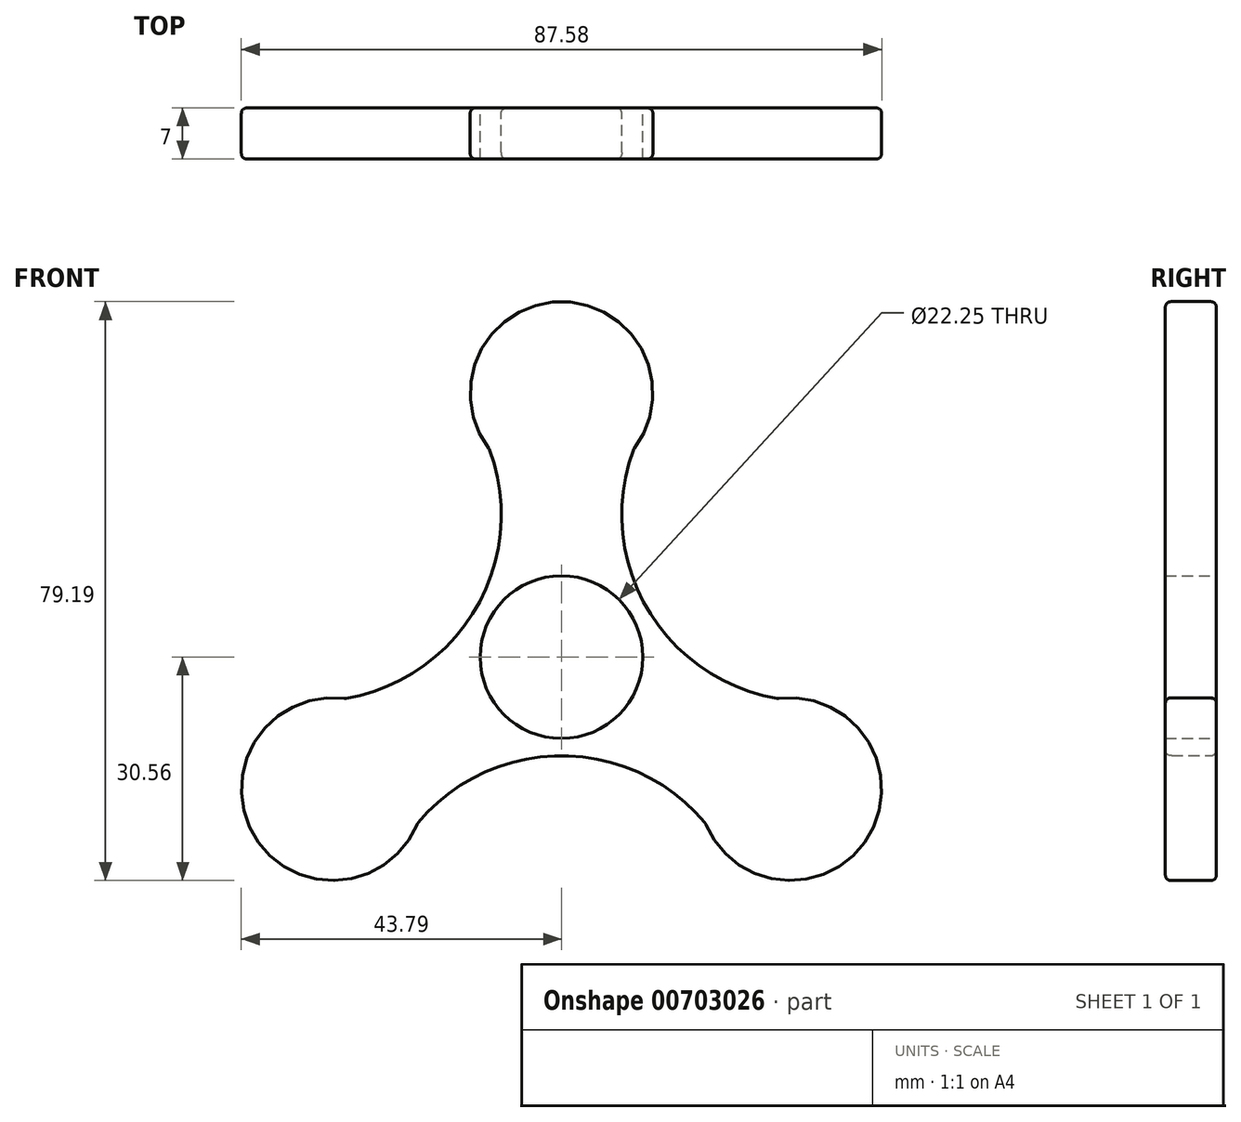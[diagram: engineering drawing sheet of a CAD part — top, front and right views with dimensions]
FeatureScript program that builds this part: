
annotation { "Feature Type Name" : "Feature", "Feature Type Description" : "" }
export const myFeature = defineFeature(function(context is Context, id is Id, definition is map)
    precondition{}
    {
        {
            var Q0;
            Q0=qCreatedBy(makeId("Front.planeOp"),FACE);
            var sketch = newSketch(context, id + "F0", { "sketchPlane" : qUnion([Q0])});
            skCircle(sketch, "E0", {"center": v(0, 0) * mm, "radius": 11.12 * mm});
            skCircle(sketch, "E1", {"center": v(0, 36.13) * mm, "radius": 11.12 * mm});
            skCircle(sketch, "E2", {"center": v(-31.29, -18.06) * mm, "radius": 11.12 * mm});
            skCircle(sketch, "E3", {"center": v(31.29, -18.06) * mm, "radius": 11.12 * mm});
            skCircle(sketch, "E4", {"center": v(0, 36.13) * mm, "radius": 12.5 * mm});
            skCircle(sketch, "E5", {"center": v(31.29, -18.06) * mm, "radius": 12.5 * mm});
            skCircle(sketch, "E6", {"center": v(-31.29, -18.06) * mm, "radius": 12.5 * mm});
            skArc(sketch, "E7", {"start": v(-29.58, -5.68) * mm, "mid": v(-11.67, 6.74) * mm, "end": v(-9.87, 28.46) * mm});
            skArc(sketch, "E8", {"start": v(19.71, -22.78) * mm, "mid": v(0, -13.47) * mm, "end": v(-19.71, -22.78) * mm});
            skArc(sketch, "E9", {"start": v(9.87, 28.46) * mm, "mid": v(11.67, 6.74) * mm, "end": v(29.58, -5.68) * mm});
            skSolve(sketch);
        }
        {
            var Q0;
            Q0 = qSketchRegion(id + "F0", true);
            extrude(context, id + "F1", {"entities" : qUnion([Q0]), "depth" : 7 * mm, "offsetDistance" : 25 * mm});
        }
        {
            var Q0;
            Q0=makeQuery(id+"F1.opExtrude","SWEPT_FACE",FACE,{"disambiguationData":[OSD([sQuery(id+"F0.wireOp",EDGE,"E5")])]});
            var Q1;
            Q1=makeQuery(id+"F1.opExtrude","SWEPT_FACE",FACE,{"disambiguationData":[OSD([sQuery(id+"F0.wireOp",EDGE,"E9")])]});
            var Q2;
            Q2=makeQuery(id+"F1.opExtrude","SWEPT_FACE",FACE,{"disambiguationData":[OSD([sQuery(id+"F0.wireOp",EDGE,"E4")])]});
            var Q3;
            Q3=makeQuery(id+"F1.opExtrude","SWEPT_FACE",FACE,{"disambiguationData":[OSD([sQuery(id+"F0.wireOp",EDGE,"E7")])]});
            var Q4;
            Q4=makeQuery(id+"F1.opExtrude","SWEPT_FACE",FACE,{"disambiguationData":[OSD([sQuery(id+"F0.wireOp",EDGE,"E6")])]});
            var Q5;
            Q5=makeQuery(id+"F1.opExtrude","SWEPT_FACE",FACE,{"disambiguationData":[OSD([sQuery(id+"F0.wireOp",EDGE,"E8")])]});
            fillet(context, id + "F2", {"entities" : qUnion([Q0, Q1, Q2, Q3, Q4, Q5]), "radius" : 0.87 * mm, "rho" : 0.5, "crossSection" : FilletCrossSection.CONIC, "allowEdgeOverflow" : false});
        }
        {
            var Q0;
            Q0=makeQuery(id+"F1.opExtrude","CAP_FACE",FACE,{"disambiguationData":[OSD([sQuery(id+"F0.wireOp",EDGE,"E0"),sQuery(id+"F0.wireOp",EDGE,"E1"),sQuery(id+"F0.wireOp",EDGE,"E2"),sQuery(id+"F0.wireOp",EDGE,"E3"),sQuery(id+"F0.wireOp",EDGE,"E4"),sQuery(id+"F0.wireOp",EDGE,"E5"),sQuery(id+"F0.wireOp",EDGE,"E6"),sQuery(id+"F0.wireOp",EDGE,"E7"),sQuery(id+"F0.wireOp",EDGE,"E8"),sQuery(id+"F0.wireOp",EDGE,"E9")])],"isStart":false});
            var sketch = newSketch(context, id + "F3", { "sketchPlane" : qUnion([Q0])});
            skSolve(sketch);
        }
        {
            var Q0;
            Q0=makeQuery(id+"F0.imprint","IMPRINT",FACE,{"disambiguationData":[TD([[makeQuery(id+"F0.imprint","IMPRINT",EDGE,{"derivedFrom":sQuery(id+"F0.wireOp",EDGE,"E1")}),1.0]])]});
            extrude(context, id + "F4", {"entities" : qUnion([Q0]), "operationType" : NewBodyOperationType.ADD, "depth" : 7 * mm, "offsetDistance" : 25 * mm});
        }
        {
            var Q0;
            Q0=makeQuery(id+"F3.imprint","IMPRINT",FACE,{"disambiguationData":[TD([[makeQuery(id+"F3.imprint","IMPRINT",EDGE,{"derivedFrom":makeQuery(id+"F1.opExtrude","CAP_EDGE",EDGE,{"disambiguationData":[OSD([sQuery(id+"F0.wireOp",EDGE,"E3")])],"isStart":false})}),1.0]])]});
            extrude(context, id + "F5", {"entities" : qUnion([Q0]), "operationType" : NewBodyOperationType.ADD, "oppositeDirection" : true, "depth" : 7 * mm, "offsetDistance" : 25 * mm});
        }
        {
            var Q0;
            Q0=makeQuery(id+"F0.imprint","IMPRINT",FACE,{"disambiguationData":[TD([[makeQuery(id+"F0.imprint","IMPRINT",EDGE,{"derivedFrom":sQuery(id+"F0.wireOp",EDGE,"E2")}),1.0]])]});
            extrude(context, id + "F6", {"entities" : qUnion([Q0]), "operationType" : NewBodyOperationType.ADD, "depth" : 7 * mm, "offsetDistance" : 25 * mm});
        }
    });
